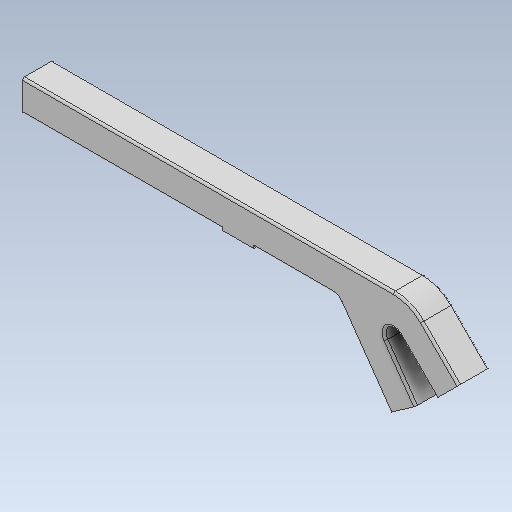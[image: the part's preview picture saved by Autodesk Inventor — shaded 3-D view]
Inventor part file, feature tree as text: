
AUTODESK INVENTOR PART (.ipt)
format: ipt  version: 2021 (Build 250183000, 183)  size: 257,024 bytes
history: native  units: mm
features: extrude x5, sketch x4, fillet x3
ambient origin geometry x8: Origin, YZ Plane, XZ Plane, XY Plane, X Axis, Y Axis, Z Axis, Center Point
bodies: Solid1 (feature_tree)
feature tree (12):
  extrude  "Extrusion1"  Depth=30.0mm
  extrude  "Extrusion4"  Depth=9.0mm
  fillet  "Fillet1"  Radius=30.0mm
  extrude  "Extrusion5"  Depth=9.0mm
  fillet  "Fillet2"  Radius=150.0mm
  extrude  "Extrusion6"  Depth=2.0mm
  extrude  "Extrusion7"  Depth=2.0mm
  fillet  "Fillet3"  Radius=30.0mm
  sketch  "Sketch4"  dims[d31=30.0mm d32=0.0mm d38=30.0mm]
  sketch  "Sketch5"  dims[d39=30.0mm d40=9.0mm d47=30.0mm]
  sketch  "Sketch6"  dims[d53=9.0mm d56=300.0mm d58=150.0mm]
  sketch  "Sketch7"  dims[d59=50.0mm d60=6.108652mm d61=75.0mm d62=30.0mm d63=15.0mm d64=1.0mm d65=30.0mm d66=0.0mm d67=2.0mm d68=2.5mm d69=2.5mm d70=2.5mm d71=2.5mm d72=350.0mm d73=0.0mm d74=2.0mm d75=2.5mm d76=2.5mm d77=2.5mm d78=2.5mm d79=50.0mm d80=0.0mm d81=2.5mm d82=2.5mm d83=2.5mm d84=2.5mm d85=50.0mm d86=0.0mm d87=2.0mm d88=45.0deg]
